# Revit family: IS_TonicII_R4305_BIM_GB
name_source: partatom
category: Plumbing Fixtures
revit_build: Autodesk Revit MEP 2014 (Build: 20140709_2115(x64)
units: mm (PartAtom-declared; Revit-internal decimal feet)

## types (5) — shared parameters
Accessories = www.idealspec.co.uk
AreaUnits = millimeters
Assembly Code = C1030200
AssetType = Fixed
BREEAM = No
Brand = Ideal Standard
Category = Furniture
CodePerformance = EN 14749:2005
ConnectionType = Plumbing
Default Elevation = 800 mm  [stored 2.62467 ft]
Description = Tonic II 1200mm wall hung washbasin unit with 2 drawers
DurationUnit = year
ECA = No
ExpectedLife = 30
Features = 1200mm wall hung washbasin unit with 2 drawers
HandleMatl = ISI_IdealStandard_Handle_Silver_Render
IfcExportAs = IfcFurnitureType
IfcExportType = USERDEFINED
InstallationInstructions = www.idealspec.co.uk/resources.html
LinearUnits = millimeters
Manufacturer = Ideal Standard (UK) Ltd
ManufacturerURL = www.idealspec.co.uk
ModelReference = Tonic II 1200mm wall hung washbasin unit with 2 drawers
NBSDescription = Bathroom integrated duct work
NBSReference = 45-35-72/320
NettWeight = 27 Kg
NominalDepth = 440 mm  [stored 1.44357 ft]
NominalHeight = 360 mm  [stored 1.1811 ft]
NominalLength = 440 mm  [stored 1.44357 ft]
NominalWidth = 1200 mm
Shape = Rectangular
Size = 360 x 440 x 1200 mm
Space = Internal
SpareParts = www.fastpart-spares.co.uk
TMV3 = No
URL = www.idealspec.co.uk
Uniclass2015Description = Bathroom integrated duct work
Uniclass2015Reference = Pr_40_30_78_04
Uniclass2015Version = Products v1.1
Version = 1
VolumeUnits = Litres
WRAS = No
WarrantyDescription = Manufacturers Warranty
WarrantyDurationParts = 5
WarrantyDurationUnit = year
WaterEfficientProduct = No
zero-valued in all types: CWFU, Cost, HWFU

## per-type parameters (varying)
| type | BIMObjectName | BarCode | Color | Finish | LaminateFinish | Model | ModelNumber | Name | ProductInformation |
| R4305FE - Tonic II 1200mm Wall Hung Washbasin Unit - Wood Light Grey | ISI_IdealStandard_Furniture_TonicII_R4305FE | 3391500571747 | Light Grey Wood | Light Grey Wood | ISI_IdealStandard_Furniture_WoodLightGreyFE_Render | R4305FE | R4305FE | ISI_Furniture_TonicII_R4305FE_IdealStandard | www.idealspec.co.uk/datasheets/R4305FE |
| R4305FF - Tonic II 1200mm Wall Hung Washbasin Unit - Wood Light Brown | ISI_IdealStandard_Furniture_TonicII_R4305FF | 3391500571730 | Light Brown Wood | Light Brown Wood | ISI_IdealStandard_Furniture_WoodLightBrownFF_Render | R4305FF | R4305FF | ISI_Furniture_TonicII_R4305FF_IdealStandard | www.idealspec.co.uk/datasheets/R4305FF |
| R4305FA - Tonic II 1200mm Wall Hung Washbasin Unit - Gloss Light Grey | ISI_IdealStandard_Furniture_TonicII_R4305FA | 3391500571716 | Light Grey Gloss | Light Grey Gloss | ISI_IdealStandard_Furniture_GlossLightGreyFA_Render | R4305FA | R4305FA | ISI_Furniture_TonicII_R4305FA_IdealStandard | www.idealspec.co.uk/datasheets/R4305FA |
| R4305FC - Tonic II 1200mm Wall Hung Washbasin Unit - Gloss Light Brown | ISI_IdealStandard_Furniture_TonicII_R4305FC | 3391500571723 | Light Brown Gloss | Light Brown Gloss | ISI_IdealStandard_Furniture_GlossLightBrownFC_Render | R4305FC | R4305FC | ISI_Furniture_TonicII_R4305FC_IdealStandard | www.idealspec.co.uk/datasheets/R4305FC |
| R4305WG - Tonic II 1200mm Wall Hung Washbasin Unit - White Gloss | ISI_IdealStandard_Furniture_TonicII_R4305WG | 3391500571709 | Gloss White | Gloss White | ISI_IdealStandard_Furniture_GlosswhiteWG_Render | R4305WG | R4305WG | ISI_Furniture_TonicII_R4305WG_IdealStandard | www.idealspec.co.uk/datasheets/R4305WG |

note: [stored X ft] marks values corroborated as IEEE doubles in the binary element streams (Revit-internal decimal feet)

## geometry (parser evidence)
native form markers: Sweep x4
no freeform markers — native parametric forms only
